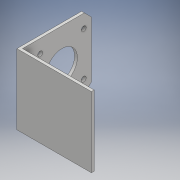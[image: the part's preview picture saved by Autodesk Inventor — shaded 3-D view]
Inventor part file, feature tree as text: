
AUTODESK INVENTOR PART (.ipt)
format: ipt  version: 2018 (Build 220112000, 112)  size: 133,120 bytes
history: native  units: mm
features: sketch x4, extrude x3
ambient origin geometry x8: Origin, YZ Plane, XZ Plane, XY Plane, X Axis, Y Axis, Z Axis, Center Point
bodies: Solid1 (feature_tree)
feature tree (7):
  extrude  "Extrusion1"  Depth=2.0mm
  extrude  "Extrusion2"  Depth=53.0mm
  extrude  "Extrusion3"  Depth=50.0mm
  sketch  "Sketch4"  dims[d9=3.5mm d10=31.0mm d11=31.0mm d12=21.0mm d13=50.0mm d14=0.0mm d15=45.0deg d16=5.0mm d17=50.0mm d18=0.0mm]
  sketch  "Sketch1"  dims[d1=51.0mm d2=2.0mm]
  sketch  "Sketch2"  dims[d4=2.0mm d5=53.0mm]
  sketch  "Sketch3"  dims[d6=50.0mm d7=0.0mm d8=22.1mm]
